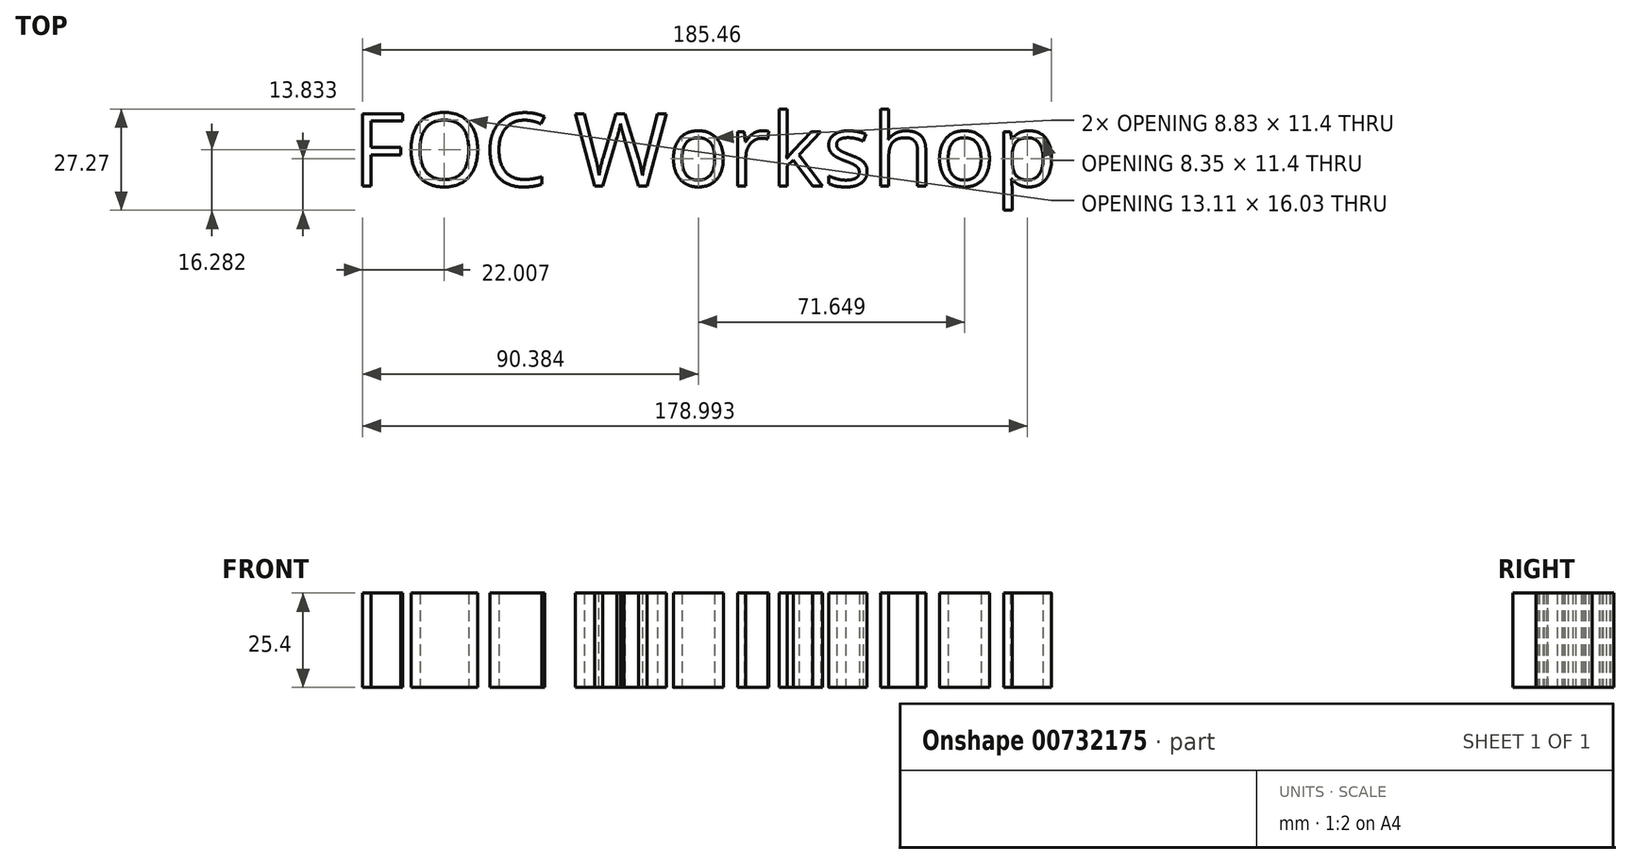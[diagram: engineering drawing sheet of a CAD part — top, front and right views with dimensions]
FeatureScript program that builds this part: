
annotation { "Feature Type Name" : "Feature", "Feature Type Description" : "" }
export const myFeature = defineFeature(function(context is Context, id is Id, definition is map)
    precondition{}
    {
        {
            var Q0;
            Q0=qCreatedBy(makeId("Top.planeOp"),FACE);
            var sketch = newSketch(context, id + "F0", { "sketchPlane" : qUnion([Q0])});
            skText(sketch, "E0", { "text": "FOC Workshop", "fontName": "OpenSans-Regular.ttf"});
            const initialGuessF0  = {"E0": [-0.06854, 0.08315, 1, 0, 0.01963]};
            skSetInitialGuess(sketch, initialGuessF0);
            skSolve(sketch);
        }
        {
            var Q0;
            Q0 = qSketchRegion(id + "F0", true);
            extrude(context, id + "F1", {"entities" : qUnion([Q0]), "depth" : 25.4 * mm, "offsetDistance" : 25.4 * mm});
        }
    });
